# Revit family: Shower-Valve_Trim-KOHLER-Singulier-K-TS10448
name_source: partatom
category: Specialty Equipment
revit_build: Autodesk Revit 2015 (Build: 20140606_1530(x64)
units: mm (PartAtom-declared; Revit-internal decimal feet)

## types (1)
- CP-Polished Chrome
    ADA Compliant = Yes
    Assembly Code = C1030200
    Date Modified = 02/13/2019
    Default Elevation = 42"
    Description = Rite-Temp valve trim with lever handle
    Finish = Kohler-Metal-CP-Polished_Chrome
    Handle Clearance = 3 1/2"
    Height = 7 3/16"
    Length = 4 5/16"
    Manufacturer = KOHLER Co.
    MasterFormat 1995 = 10820
    MasterFormat 2004 = 10.28.13
    Material = Premium Metal Construction
    Model = K-TS10448-4-CP
    Product Documentation Link = https://www.us.kohler.com
    Product Name = Singulier
    Product Page URL = http://www.us.kohler.com
    URL = https://www.us.kohler.com
    WaterSense Certified = No
    Width = 6 3/8"

## geometry (parser evidence)
native form markers: Sweep x6
no freeform markers — native parametric forms only
